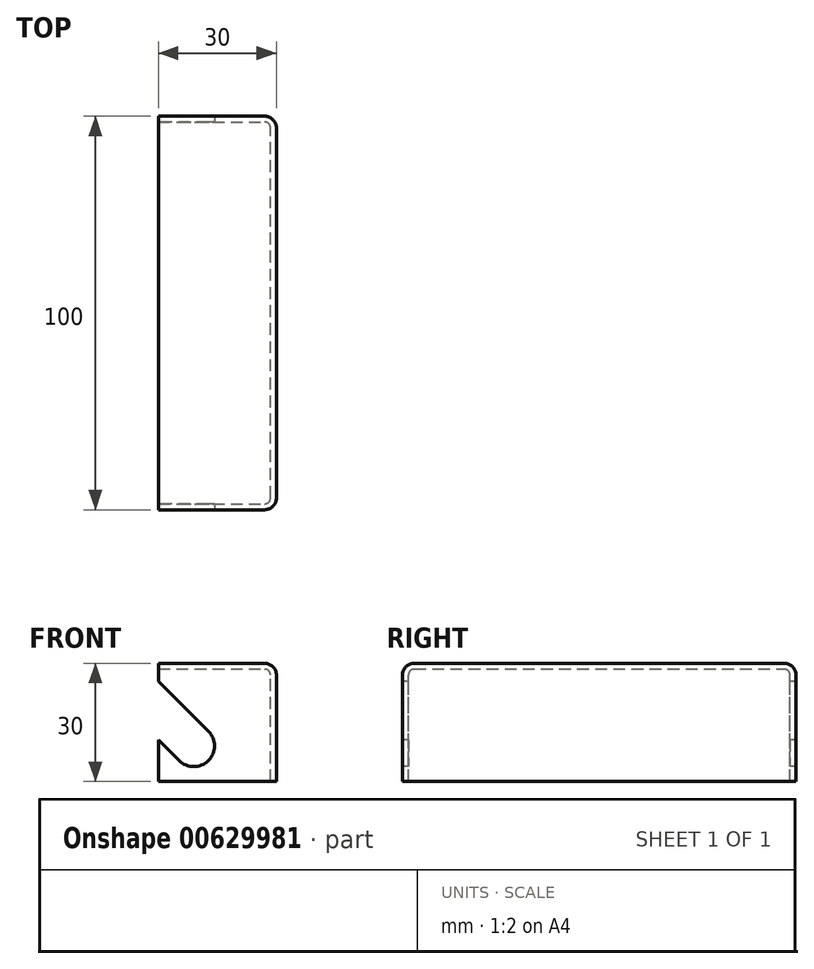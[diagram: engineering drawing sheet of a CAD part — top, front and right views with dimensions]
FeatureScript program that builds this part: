
annotation { "Feature Type Name" : "Feature", "Feature Type Description" : "" }
export const myFeature = defineFeature(function(context is Context, id is Id, definition is map)
    precondition{}
    {
        {
            var Q0;
            Q0=qCreatedBy(makeId("Front.planeOp"),FACE);
            var sketch = newSketch(context, id + "F0", { "sketchPlane" : qUnion([Q0])});
            skLineSegment(sketch, "E0.bottom", {"start": v(-15, -15) * mm, "end": v(15, -15) * mm});
            skLineSegment(sketch, "E0.top", {"start": v(-15, 15) * mm, "end": v(15, 15) * mm});
            skLineSegment(sketch, "E0.left", {"start": v(-15, -15) * mm, "end": v(-15, 15) * mm});
            skLineSegment(sketch, "E0.right", {"start": v(15, -15) * mm, "end": v(15, 15) * mm});
            skLineSegment(sketch, "E1", {"start": v(15, 0) * mm, "end": v(0, 0) * mm, "construction": true});
            skLineSegment(sketch, "E2", {"start": v(0, -15) * mm, "end": v(0, 0) * mm, "construction": true});
            skSolve(sketch);
        }
        {
            var Q0;
            Q0 = qSketchRegion(id + "F0", true);
            extrude(context, id + "F1", {"entities" : qUnion([Q0]), "depth" : 50 * mm, "offsetDistance" : 25.4 * mm, "hasSecondDirection" : true, "secondDirectionOppositeDirection" : true, "secondDirectionDepth" : 50 * mm});
        }
        {
            var Q0;
            Q0=makeQuery(id+"F1.opExtrude","CAP_EDGE",EDGE,{"disambiguationData":[OSD([sQuery(id+"F0.wireOp",EDGE,"E0.top")])],"isStart":false});
            var Q1;
            Q1=makeQuery(id+"F1.opExtrude","CAP_EDGE",EDGE,{"disambiguationData":[OSD([sQuery(id+"F0.wireOp",EDGE,"E0.top")])],"isStart":true});
            var Q2;
            Q2=makeQuery(id+"F1.opExtrude","SWEPT_EDGE",EDGE,{"disambiguationData":[OSD([sQuery(id+"F0.wireOp",EDGE,"E0.top"),sQuery(id+"F0.wireOp",EDGE,"E0.right")])]});
            var Q3;
            Q3=makeQuery(id+"F1.opExtrude","CAP_EDGE",EDGE,{"disambiguationData":[OSD([sQuery(id+"F0.wireOp",EDGE,"E0.right")])],"isStart":false});
            var Q4;
            Q4=makeQuery(id+"F1.opExtrude","CAP_EDGE",EDGE,{"disambiguationData":[OSD([sQuery(id+"F0.wireOp",EDGE,"E0.right")])],"isStart":true});
            fillet(context, id + "F2", {"entities" : qUnion([Q0, Q1, Q2, Q3, Q4]), "radius" : 3 * mm, "tangentPropagation" : true, "allowEdgeOverflow" : false});
        }
        {
            var Q0;
            Q0=makeQuery(id+"F1.opExtrude","SWEPT_FACE",FACE,{"disambiguationData":[OSD([sQuery(id+"F0.wireOp",EDGE,"E0.left")])]});
            var Q1;
            Q1=makeQuery(id+"F1.opExtrude","SWEPT_FACE",FACE,{"disambiguationData":[OSD([sQuery(id+"F0.wireOp",EDGE,"E0.bottom")])]});
            shell(context, id + "F3", {"entities" : qUnion([Q0, Q1]), "thickness" : 1.5 * mm});
        }
        {
            var Q0;
            Q0=makeQuery(id+"F1.opExtrude","CAP_FACE",FACE,{"disambiguationData":[OSD([sQuery(id+"F0.wireOp",EDGE,"E0.bottom"),sQuery(id+"F0.wireOp",EDGE,"E0.top"),sQuery(id+"F0.wireOp",EDGE,"E0.left"),sQuery(id+"F0.wireOp",EDGE,"E0.right")])],"isStart":false});
            var sketch = newSketch(context, id + "F4", { "sketchPlane" : qUnion([Q0])});
            skArc(sketch, "E3", {"start": v(-9.71, -9.71) * mm, "mid": v(-2.29, -9.71) * mm, "end": v(-2.29, -2.29) * mm});
            skLineSegment(sketch, "E4", {"start": v(-2.29, -2.29) * mm, "end": v(-15, 10.42) * mm});
            skLineSegment(sketch, "E5", {"start": v(-15, 10.42) * mm, "end": v(-15, -4.42) * mm});
            skLineSegment(sketch, "E6", {"start": v(-15, -4.42) * mm, "end": v(-9.71, -9.71) * mm});
            skLineSegment(sketch, "E7", {"start": v(-9.71, -9.71) * mm, "end": v(-2.29, -2.29) * mm, "construction": true});
            skSolve(sketch);
        }
        {
            var Q0;
            Q0 = qSketchRegion(id + "F4", true);
            extrude(context, id + "F5", {"entities" : qUnion([Q0]), "operationType" : NewBodyOperationType.REMOVE, "endBound" : BoundingType.THROUGH_ALL, "oppositeDirection" : true, "depth" : 25 * mm, "offsetDistance" : 25 * mm});
        }
    });
